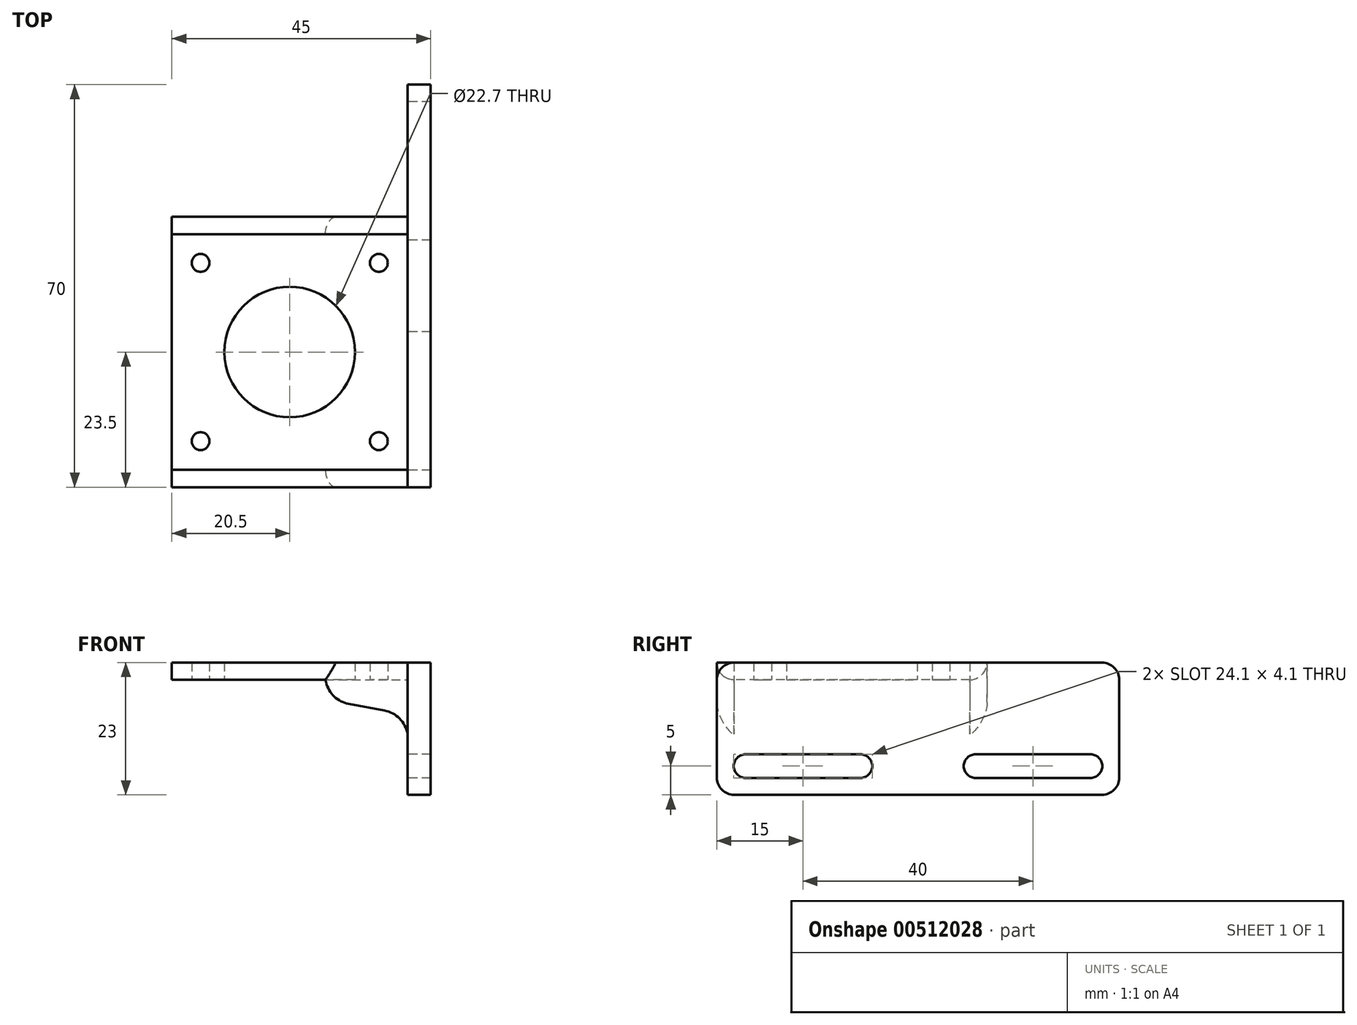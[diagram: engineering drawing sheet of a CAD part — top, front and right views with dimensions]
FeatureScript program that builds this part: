
annotation { "Feature Type Name" : "Feature", "Feature Type Description" : "" }
export const myFeature = defineFeature(function(context is Context, id is Id, definition is map)
    precondition{}
    {
        {
            var Q0;
            Q0=qCreatedBy(makeId("Top.planeOp"),FACE);
            var sketch = newSketch(context, id + "F0", { "sketchPlane" : qUnion([Q0])});
            skLineSegment(sketch, "E0.bottom", {"start": v(-20.5, 20.5) * mm, "end": v(20.5, 20.5) * mm});
            skLineSegment(sketch, "E0.top", {"start": v(-20.5, -20.5) * mm, "end": v(20.5, -20.5) * mm});
            skLineSegment(sketch, "E0.left", {"start": v(-20.5, 20.5) * mm, "end": v(-20.5, -20.5) * mm});
            skLineSegment(sketch, "E0.right", {"start": v(20.5, 20.5) * mm, "end": v(20.5, -20.5) * mm});
            skLineSegment(sketch, "E1", {"start": v(0, 20.5) * mm, "end": v(0, -20.5) * mm, "construction": true});
            skLineSegment(sketch, "E2", {"start": v(15.5, 20.5) * mm, "end": v(15.5, -20.5) * mm, "construction": true});
            skLineSegment(sketch, "E3", {"start": v(-15.5, 20.5) * mm, "end": v(-15.5, -20.5) * mm, "construction": true});
            skLineSegment(sketch, "E4", {"start": v(-20.5, 15.5) * mm, "end": v(20.5, 15.5) * mm, "construction": true});
            skLineSegment(sketch, "E5", {"start": v(-20.5, -15.5) * mm, "end": v(20.5, -15.5) * mm, "construction": true});
            skLineSegment(sketch, "E6", {"start": v(20.5, 0) * mm, "end": v(-20.5, 0) * mm, "construction": true});
            skCircle(sketch, "E7", {"center": v(0, 0) * mm, "radius": 11.35 * mm});
            skLineSegment(sketch, "E8", {"start": v(7, 15.5) * mm, "end": v(7, 0) * mm});
            skLineSegment(sketch, "E9", {"start": v(5.1, 0) * mm, "end": v(5.1, -15.5) * mm});
            skLineSegment(sketch, "E10", {"start": v(-15.5, 5.7) * mm, "end": v(0, 5.7) * mm});
            skLineSegment(sketch, "E11", {"start": v(0, 3.82) * mm, "end": v(15.5, 3.82) * mm});
            skCircle(sketch, "E12", {"center": v(-15.5, 15.5) * mm, "radius": 1.55 * mm});
            skCircle(sketch, "E13", {"center": v(15.5, 15.5) * mm, "radius": 1.55 * mm});
            skCircle(sketch, "E14", {"center": v(15.5, -15.5) * mm, "radius": 1.55 * mm});
            skCircle(sketch, "E15", {"center": v(-15.5, -15.5) * mm, "radius": 1.55 * mm});
            skSolve(sketch);
        }
        {
            var Q0;
            Q0 = qSketchRegion(id + "F0", true);
            extrude(context, id + "F1", {"entities" : qUnion([Q0]), "depth" : 3 * mm});
        }
        {
            var Q0;
            Q0=makeQuery(id+"F1.opExtrude","SWEPT_FACE",FACE,{"disambiguationData":[OSD([sQuery(id+"F0.wireOp",EDGE,"E0.right")])]});
            var sketch = newSketch(context, id + "F2", { "sketchPlane" : qUnion([Q0])});
            skLineSegment(sketch, "E16.bottom", {"start": v(-23.5, 3) * mm, "end": v(46.5, 3) * mm});
            skLineSegment(sketch, "E16.top", {"start": v(-23.5, -20) * mm, "end": v(46.5, -20) * mm});
            skLineSegment(sketch, "E16.left", {"start": v(-23.5, 3) * mm, "end": v(-23.5, -20) * mm});
            skLineSegment(sketch, "E16.right", {"start": v(46.5, 3) * mm, "end": v(46.5, -20) * mm});
            skCircle(sketch, "E17", {"center": v(-18.5, -15) * mm, "radius": 2.05 * mm});
            skCircle(sketch, "E18", {"center": v(41.5, -15) * mm, "radius": 2.05 * mm});
            skLineSegment(sketch, "E19", {"start": v(-18.5, -12.95) * mm, "end": v(41.5, -12.95) * mm});
            skLineSegment(sketch, "E20", {"start": v(-18.5, -17.05) * mm, "end": v(41.5, -17.05) * mm});
            skArc(sketch, "E21", {"start": v(21.5, -12.95) * mm, "mid": v(19.45, -15) * mm, "end": v(21.5, -17.05) * mm});
            skArc(sketch, "E22", {"start": v(1.5, -17.05) * mm, "mid": v(3.55, -15) * mm, "end": v(1.5, -12.95) * mm});
            skSolve(sketch);
        }
        {
            var Q0;
            Q0 = qSketchRegion(id + "F2", true);
            var Q1;
            {var subQ0=sQuery(id+"F2.wireOp",EDGE,"E21");Q1=makeQuery(id+"F2.imprint","IMPRINT",FACE,{"disambiguationData":[TD([[makeQuery(id+"F2.imprint","IMPRINT",EDGE,{"derivedFrom":subQ0}),-1.0]])]});}
            extrude(context, id + "F3", {"entities" : qUnion([Q0, Q1]), "depth" : 4 * mm});
        }
        {
            var Q0;
            Q0=makeQuery(id+"F3.opExtrude","SWEPT_EDGE",EDGE,{"disambiguationData":[OSD([sQuery(id+"F2.wireOp",EDGE,"E16.top"),sQuery(id+"F2.wireOp",EDGE,"E16.right")])]});
            var Q1;
            Q1=makeQuery(id+"F3.opExtrude","SWEPT_EDGE",EDGE,{"disambiguationData":[OSD([sQuery(id+"F2.wireOp",EDGE,"E16.top"),sQuery(id+"F2.wireOp",EDGE,"E16.left")])]});
            var Q2;
            Q2=makeQuery(id+"FFNxEOOAgJ8R9Dv_2.opPattern","COPY",EDGE,{"derivedFrom":makeQuery(id+"FAvmf0ZsXksJTnV_1.opExtrude","CAP_EDGE",EDGE,{"disambiguationData":[OSD([sQuery(id+"F0.wireOp",EDGE,"E0.bottom")])],"isStart":false}),"instanceName":"1"});
            var Q3;
            Q3=makeQuery(id+"F3.opExtrude","SWEPT_EDGE",EDGE,{"disambiguationData":[OSD([sQuery(id+"F2.wireOp",EDGE,"E16.bottom"),sQuery(id+"F2.wireOp",EDGE,"E16.right")])]});
            var Q4;
            Q4=makeQuery(id+"F3.opExtrude","SWEPT_EDGE",EDGE,{"disambiguationData":[OSD([sQuery(id+"F2.wireOp",EDGE,"E16.bottom"),sQuery(id+"F2.wireOp",EDGE,"E16.left")])]});
            var Q5;
            Q5=makeQuery(id+"FFNxEOOAgJ8R9Dv_2.opPattern","COPY",EDGE,{"derivedFrom":makeQuery(id+"FAvmf0ZsXksJTnV_1.opExtrude","CAP_EDGE",EDGE,{"disambiguationData":[OSD([sQuery(id+"FGpwWgO6UiPWsFZ_1.wireOp",EDGE,"8SjgC7Pj-3DIV-6jF1-kdcX-FBYk4W7JzsZ4")])],"isStart":false}),"instanceName":"1"});
            var Q6;
            Q6=makeQuery(id+"FAvmf0ZsXksJTnV_1.opExtrude","CAP_EDGE",EDGE,{"disambiguationData":[OSD([sQuery(id+"FGpwWgO6UiPWsFZ_1.wireOp",EDGE,"8SjgC7Pj-3DIV-6jF1-kdcX-FBYk4W7JzsZ4")])],"isStart":false});
            var Q7;
            Q7=makeQuery(id+"FAvmf0ZsXksJTnV_1.opExtrude","CAP_EDGE",EDGE,{"disambiguationData":[OSD([sQuery(id+"F0.wireOp",EDGE,"E0.bottom")])],"isStart":false});
            fillet(context, id + "F4", {"entities" : qUnion([Q0, Q1, Q2, Q3, Q4, Q5, Q6, Q7]), "radius" : 3 * mm, "tangentPropagation" : true, "allowEdgeOverflow" : false});
        }
        {
            var Q0;
            Q0=makeQuery(id+"F1.opExtrude","SWEPT_FACE",FACE,{"disambiguationData":[OSD([sQuery(id+"F0.wireOp",EDGE,"E0.top")])]});
            var sketch = newSketch(context, id + "F5", { "sketchPlane" : qUnion([Q0])});
            skLineSegment(sketch, "E23", {"start": v(10.3, -4.2) * mm, "end": v(16.47, -5.34) * mm});
            skLineSegment(sketch, "E24", {"start": v(20.5, -6.08) * mm, "end": v(20.5, 0) * mm});
            skPoint(sketch, "E25.visualSharp", {"position": v(-21.99, 1.74) * mm});
            skPoint(sketch, "E26.visualSharp", {"position": v(20.5, -6.08) * mm});
            skArc(sketch, "E26.filletArc", {"start": v(20.5, -11.08) * mm, "mid": v(19.66, -7.38) * mm, "end": v(16.47, -5.34) * mm});
            skArc(sketch, "E27.filletArc", {"start": v(6.33, -0.43) * mm, "mid": v(7.75, -2.9) * mm, "end": v(10.3, -4.2) * mm});
            skArc(sketch, "E28.filletArc", {"start": v(6.33, -0.43) * mm, "mid": v(4.9, 2.04) * mm, "end": v(2.37, 3.34) * mm});
            skLineSegment(sketch, "E29", {"start": v(20.5, -6.08) * mm, "end": v(20.5, -11.08) * mm});
            skSolve(sketch);
        }
        {
            var Q0;
            Q0 = qSketchRegion(id + "F5", true);
            var Q1;
            Q1=makeQuery(id+"F5.imprint","IMPRINT",FACE,{"disambiguationData":[TD([[makeQuery(id+"F5.imprint","IMPRINT",EDGE,{"derivedFrom":sQuery(id+"F5.wireOp",EDGE,"E23")}),1.0]])]});
            var Q2;
            {var subQ0=sQuery(id+"F0.wireOp",EDGE,"E0.top");Q2=makeQuery(id+"F5.imprint","IMPRINT",FACE,{"disambiguationData":[TD([[makeQuery(id+"F5.imprint","IMPRINT",EDGE,{"derivedFrom":makeQuery(id+"F1.opExtrude","CAP_EDGE",EDGE,{"disambiguationData":[OSD([subQ0])],"isStart":false})}),-1.0]])]});}
            extrude(context, id + "F6", {"entities" : qUnion([Q0, Q1, Q2]), "depth" : 3 * mm});
        }
        {
            var Q0;
            {var subQ0=sQuery(id+"F0.wireOp",EDGE,"E0.top");var subQ1=makeQuery(id+"F1.opExtrude","CAP_EDGE",EDGE,{"disambiguationData":[OSD([subQ0])],"isStart":true});Q0=makeQuery(id+"F6.opExtrude","CAP_EDGE",EDGE,{"disambiguationData":[OSD([subQ0]),TDD([makeQuery(id+"F5.imprint","IMPRINT",EDGE,{"disambiguationData":[TD([[makeQuery(id+"F5.imprint","INTERSECT",VERTEX,{"derivedFrom":[subQ1,sQuery(id+"F5.wireOp",EDGE,"E28.filletArc")]}),1.0]])],"derivedFrom":subQ1})])],"isStart":false});}
            var Q1;
            Q1=makeQuery(id+"F6.opExtrude","CAP_EDGE",EDGE,{"disambiguationData":[OSD([sQuery(id+"F5.wireOp",EDGE,"E27.filletArc")])],"isStart":false});
            var Q2;
            Q2=makeQuery(id+"F6.opExtrude","CAP_EDGE",EDGE,{"disambiguationData":[OSD([sQuery(id+"F5.wireOp",EDGE,"E23")])],"isStart":false});
            var Q3;
            {var subQ0=sQuery(id+"F5.wireOp",EDGE,"E26.filletArc");Q3=makeQuery(id+"F6.opExtrude","CAP_EDGE",EDGE,{"disambiguationData":[OSD([subQ0]),TDD([makeQuery(id+"F5.imprint","IMPRINT",EDGE,{"disambiguationData":[TD([[makeQuery(id+"F5.imprint","INTERSECT",VERTEX,{"derivedFrom":[sQuery(id+"F5.wireOp",EDGE,"E23"),subQ0]}),1.0]])],"derivedFrom":subQ0})])],"isStart":false});}
            fillet(context, id + "F7", {"entities" : qUnion([Q0, Q1, Q2, Q3]), "radius" : 3 * mm, "tangentPropagation" : true, "allowEdgeOverflow" : false});
        }
        {
            var Q0;
            Q0=makeQuery(id+"F6.opExtrude","SWEPT_BODY",BODY,{"disambiguationData":[OSD([sQuery(id+"F0.wireOp",EDGE,"E0.top"),sQuery(id+"F0.wireOp",EDGE,"E0.left"),sQuery(id+"F0.wireOp",EDGE,"E0.right"),sQuery(id+"F5.wireOp",EDGE,"E23"),sQuery(id+"F5.wireOp",EDGE,"E24"),sQuery(id+"F5.wireOp",EDGE,"E26.filletArc"),sQuery(id+"F5.wireOp",EDGE,"E27.filletArc"),sQuery(id+"F5.wireOp",EDGE,"E28.filletArc"),sQuery(id+"F5.wireOp",EDGE,"E29")])]});
            var Q1;
            Q1=qCreatedBy(makeId("Front.planeOp"),FACE);
            mirror(context, id + "F8", {"entities" : qUnion([Q0]), "mirrorPlane" : qUnion([Q1])});
        }
        {
            var Q0;
            Q0=makeQuery(id+"F6.opExtrude","SWEPT_BODY",BODY,{"disambiguationData":[OSD([sQuery(id+"F5.wireOp",EDGE,"E26.filletArc"),sQuery(id+"F5.wireOp",EDGE,"E29")])]});
            deleteBodies(context, id + "F9", {"entities" : qUnion([Q0])});
        }
    });
